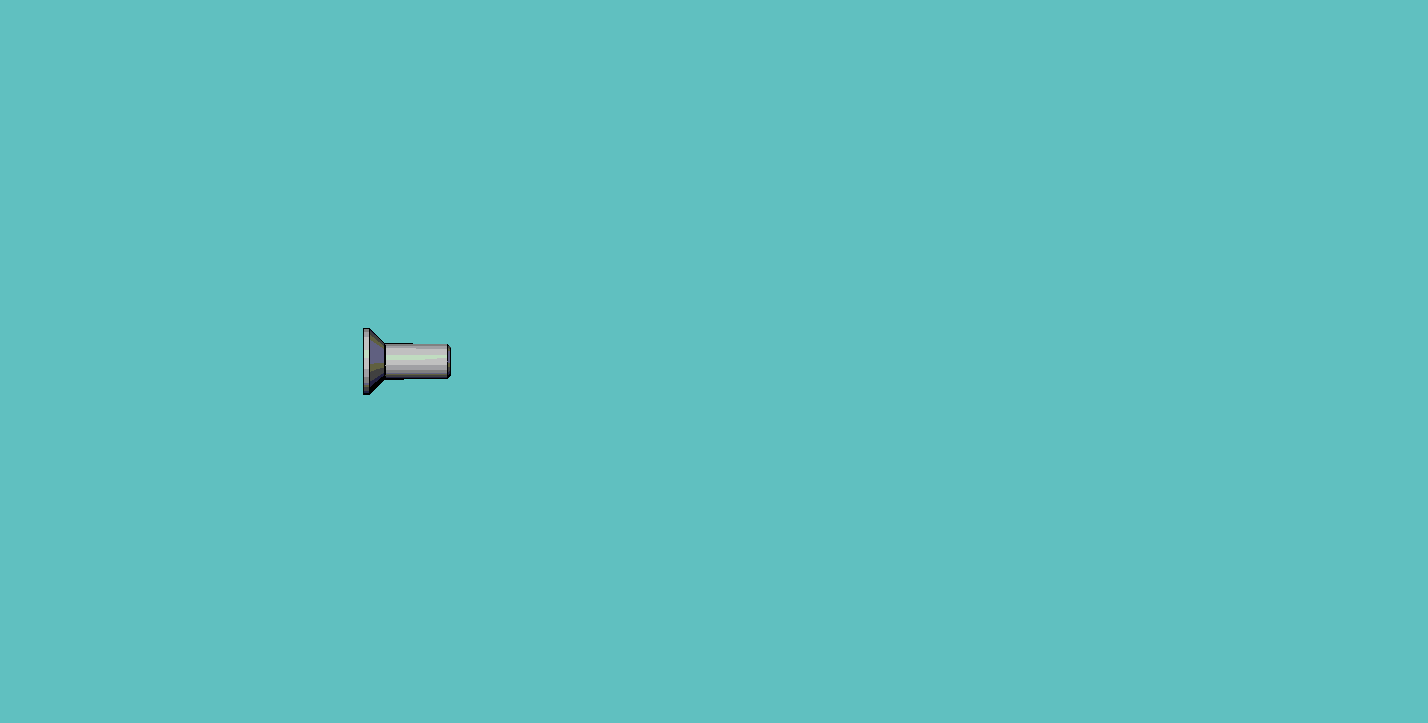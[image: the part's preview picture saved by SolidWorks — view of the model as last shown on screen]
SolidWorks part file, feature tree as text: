
SOLIDWORKS PART (.sldprt)
format: sldprt  version: not decoded by parser v0  size: 178,688 bytes
history: native  units: mm
features: sketch x4, plane x3, cut_revolve x2, material x1, revolve x1, thread x1, fillet x1, cut_extrude x1, pattern_linear x1 (+10 scaffold rows collapsed; 1 parser-record rows omitted)
feature tree (26):
  scaffold x10  (default folders/planes/origin — collapsed)
  material  "Material <not specified>"
  plane  "Plane1"
  plane  "Plane2"
  plane  "Plane3"
  parser-record x1  (decoder bookkeeping rows leaked as tree rows — omitted from the tree; the rows remain in map.json)
  revolve  "BaseBody"  [1 undecoded]
  sketch  "BodySke"  dims[c1.Head_fillet_rad=1.016mm c1.D1=19.05mm c1.Diameter=25.4mm c1.D3=50.8mm c1.D4=22.225mm c2.D4=45.0deg c2.D5=22.225mm c2.Head_ht=25.4mm c2.Length=76.2mm c2.D8=9.525mm c3.D8=45.0deg c3.D1=9.525mm c4.D8=9.525mm c5.D8=45.0deg c5.D1=73.025mm c6.D1=45.0deg c7.D1=9.525mm c8.D1=45.0deg c8.D4=22.225mm c9.D4=45.0deg c9.Thread_min=12.7mm c10.D4=9.525mm c10.Body_ch_ang=45.0deg c10.D8=22.225mm c11.D8=45.0deg c11.D5=22.225mm c12.D5=45.0deg c13.D5=~4.490128mm c14.D5=45.0deg c14.Head_dia=50.8mm c15.D5=~8.980256mm c15.Head_ch_ang=45.0deg c15.Head_side_ht=22.86mm c15.D9=19.05mm c15.Diameter=4.0mm c15.Head_dia=38.1mm c15.Minor_dia=3.22mm c16.Head_dia=7.53mm c16.D1=0.127mm c16.D2=~17.32023mm c16.Head_ang=90.0deg c16.Length=10.0mm c16.Head_ht=13.716mm c17.D1=0.715mm c17.Advance=0.7mm c17.Thread_nom=10.0mm c17.Thread_lim=~60.962186mm c17.Head_ht=2.48mm]
  thread  "ThreadCosmetic"  Diameter=5.42mm Thread_length=5.42mm Thread_minor=3.22mm  [1 undecoded]
  fillet  "Fillet1"  Radius=0.2mm
  sketch  "Sketch2"  dims[c1.D1=7.9375mm c1.D2=25.4mm c2.D2=60.0deg c2.Wall_thickness=12.827mm c2.PreBroach_depth=1.5mm c2.PreBroach_dia=2.5mm]
  cut_revolve  "PreBroach"  Angle=360deg
  sketch  "Sketch3"  dims[c1.D1=9.525mm c1.D2=9.525mm c1.Hex_size=19.05mm c1.D4=~14.664697mm c2.D4=120.0deg c2.Hex_size=15.875mm c2.D1=7.9375mm c2.D2=7.9375mm c2.D3=~13.528644mm c3.D3=120.0deg c3.D4=15.875mm c3.Hex_size=2.5mm c3.D1=1.25mm c3.D2=1.25mm c4.D3=2.5mm]
  cut_extrude  "Hex"  Depth=1.5mm Key_eng=1.5mm
  sketch  "ThdSchSke"  dims[c1.Thread_minor=~1.03886mm c1.Diameter=~1.413535mm c1.Start=~0.988134mm c1.D4=~4.446753mm c1.Vee=60.0deg c2.Thread_minor=~1.03886mm c2.Start=~2.540025mm c2.D1=~0.108159mm c2.D2=~0.108159mm c3.D1=~0.216319mm c3.SideAngle=55.0deg c3.D2=~0.216319mm c3.VeeAngle=70.0deg c3.Thread_minor=3.22mm c3.Overcut=5.0mm c3.Diameter=4.0mm c3.D6=~8.326268mm c4.D1=~8.326268mm c5.D1=90.0deg c5.Start=63.5mm c6.Start=~4.580001mm]
  cut_revolve  "ThreadSchematic"  Angle=360deg
  pattern_linear  "ThdSchPat"  Count1=8 Count2=1 Spacing1=0.6775mm Spacing2=50mm Num_threads=8 Advance=0.6775mm CopiedFlag=1
decode coverage: 10 of 11 modeling features carry decoded parameters
note: ~ marks probable driven/reference dimensions
note: 2 parameter values undecoded
note: suppression state not decoded; provenance and decode notes live in map.json
